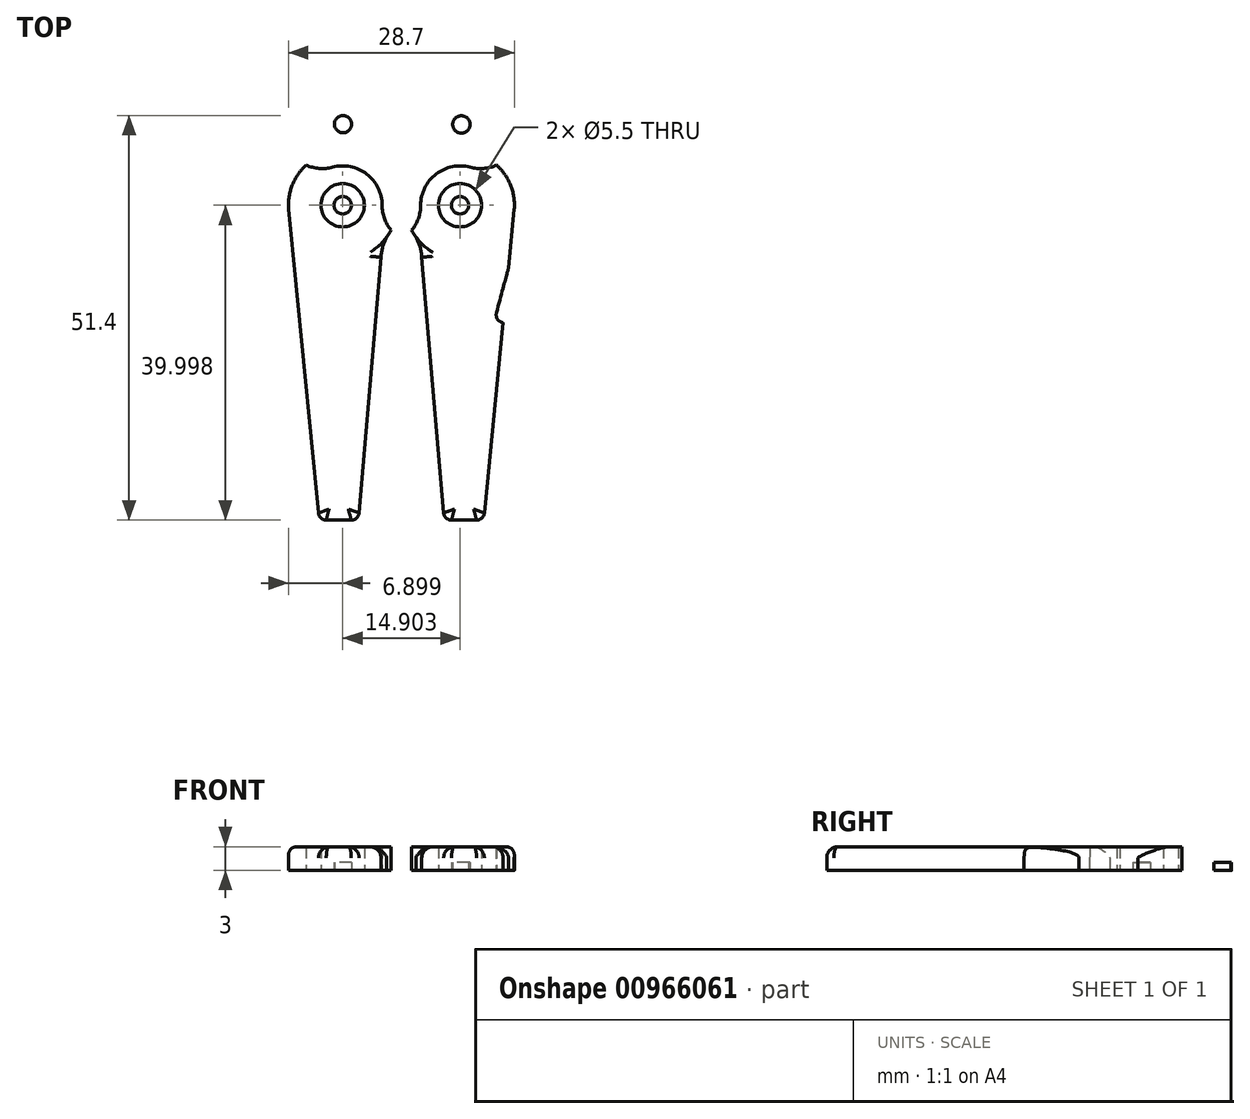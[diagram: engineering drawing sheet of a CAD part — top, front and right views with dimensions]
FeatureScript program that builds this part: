
annotation { "Feature Type Name" : "Feature", "Feature Type Description" : "" }
export const myFeature = defineFeature(function(context is Context, id is Id, definition is map)
    precondition{}
    {
        {
            var Q0;
            Q0=qCreatedBy(makeId("Top.planeOp"),FACE);
            var sketch = newSketch(context, id + "F0", { "sketchPlane" : qUnion([Q0])});
            skArc(sketch, "E0", {"start": v(1.32, 9.18) * mm, "mid": v(2.16, 10.67) * mm, "end": v(2.45, 12.35) * mm});
            skArc(sketch, "E1", {"start": v(1.32, 9.18) * mm, "mid": v(1.57, 8.73) * mm, "end": v(1.86, 8.3) * mm});
            skArc(sketch, "E2", {"start": v(2.59, 5.75) * mm, "mid": v(2.37, 7.07) * mm, "end": v(1.86, 8.3) * mm});
            skLineSegment(sketch, "E3", {"start": v(2.59, 5.75) * mm, "end": v(5.37, -26.74) * mm});
            skArc(sketch, "E4", {"start": v(5.37, -26.74) * mm, "mid": v(5.7, -27.39) * mm, "end": v(6.37, -27.65) * mm});
            skLineSegment(sketch, "E5", {"start": v(6.37, -27.65) * mm, "end": v(9.54, -27.65) * mm});
            skArc(sketch, "E6", {"start": v(9.54, -27.65) * mm, "mid": v(10.22, -27.4) * mm, "end": v(10.54, -26.75) * mm});
            skArc(sketch, "E7", {"start": v(8.75, 17.18) * mm, "mid": v(4.4, 16.31) * mm, "end": v(2.45, 12.35) * mm});
            skArc(sketch, "E8", {"start": v(14.3, 11.5) * mm, "mid": v(13.92, 14.74) * mm, "end": v(12.1, 17.45) * mm});
            skArc(sketch, "E9", {"start": v(8.75, 17.18) * mm, "mid": v(10.44, 17.02) * mm, "end": v(12.1, 17.45) * mm});
            skArc(sketch, "E10", {"start": v(12.07, -1.31) * mm, "mid": v(12.17, -2.07) * mm, "end": v(12.78, -2.54) * mm});
            skLineSegment(sketch, "E11", {"start": v(10.54, -26.75) * mm, "end": v(12.92, -2.57) * mm});
            skLineSegment(sketch, "E12", {"start": v(13.6, 4.38) * mm, "end": v(14.33, 11.86) * mm});
            skLineSegment(sketch, "E13", {"start": v(13.6, 4.38) * mm, "end": v(12.07, -1.31) * mm});
            skLineSegment(sketch, "E14", {"start": v(12.78, -2.54) * mm, "end": v(12.92, -2.57) * mm});
            skCircle(sketch, "E15", {"center": v(7.62, 22.62) * mm, "radius": 5 * mm});
            skCircle(sketch, "E16", {"center": v(7.45, 12.35) * mm, "radius": 1.1 * mm});
            skCircle(sketch, "E17", {"center": v(7.62, 22.62) * mm, "radius": 1.1 * mm});
            skArc(sketch, "E18", {"start": v(-2.45, 12.35) * mm, "mid": v(-2.16, 10.67) * mm, "end": v(-1.32, 9.18) * mm});
            skArc(sketch, "E19", {"start": v(-1.86, 8.3) * mm, "mid": v(-1.57, 8.73) * mm, "end": v(-1.32, 9.18) * mm});
            skArc(sketch, "E20", {"start": v(-1.86, 8.3) * mm, "mid": v(-2.37, 7.07) * mm, "end": v(-2.59, 5.75) * mm});
            skLineSegment(sketch, "E21", {"start": v(-2.59, 5.75) * mm, "end": v(-5.37, -26.74) * mm});
            skArc(sketch, "E22", {"start": v(-6.37, -27.65) * mm, "mid": v(-5.7, -27.39) * mm, "end": v(-5.37, -26.74) * mm});
            skLineSegment(sketch, "E23", {"start": v(-6.37, -27.65) * mm, "end": v(-9.54, -27.65) * mm});
            skLineSegment(sketch, "E24", {"start": v(-10.54, -26.75) * mm, "end": v(-14.33, 11.86) * mm});
            skArc(sketch, "E25", {"start": v(-10.54, -26.75) * mm, "mid": v(-10.22, -27.4) * mm, "end": v(-9.54, -27.65) * mm});
            skArc(sketch, "E26", {"start": v(-2.45, 12.35) * mm, "mid": v(-4.4, 16.31) * mm, "end": v(-8.75, 17.18) * mm});
            skArc(sketch, "E27", {"start": v(-12.1, 17.45) * mm, "mid": v(-13.92, 14.74) * mm, "end": v(-14.3, 11.5) * mm});
            skArc(sketch, "E28", {"start": v(-12.1, 17.45) * mm, "mid": v(-10.44, 17.02) * mm, "end": v(-8.75, 17.18) * mm});
            skCircle(sketch, "E29", {"center": v(-7.41, 22.65) * mm, "radius": 5 * mm});
            skCircle(sketch, "E30", {"center": v(-7.41, 22.65) * mm, "radius": 1.1 * mm});
            skCircle(sketch, "E31", {"center": v(-7.45, 12.35) * mm, "radius": 1.1 * mm});
            skCircle(sketch, "E32", {"center": v(-7.41, 22.65) * mm, "radius": 2.75 * mm});
            skCircle(sketch, "E33", {"center": v(-7.45, 12.35) * mm, "radius": 2.75 * mm});
            skCircle(sketch, "E34", {"center": v(7.45, 12.35) * mm, "radius": 2.75 * mm});
            skCircle(sketch, "E35", {"center": v(7.62, 22.62) * mm, "radius": 2.75 * mm});
            skSolve(sketch);
        }
        {
            var Q0;
            Q0=makeQuery(id+"F0.imprint","IMPRINT",FACE,{"disambiguationData":[TD([[makeQuery(id+"F0.imprint","IMPRINT",EDGE,{"derivedFrom":sQuery(id+"F0.wireOp",EDGE,"E18")}),-1.0]])]});
            var Q1;
            Q1=makeQuery(id+"F0.imprint","IMPRINT",FACE,{"disambiguationData":[TD([[makeQuery(id+"F0.imprint","IMPRINT",EDGE,{"derivedFrom":sQuery(id+"F0.wireOp",EDGE,"E0")}),-1.0]])]});
            var Q2;
            Q2=makeQuery(id+"F0.imprint","IMPRINT",FACE,{"disambiguationData":[TD([[makeQuery(id+"F0.imprint","IMPRINT",EDGE,{"derivedFrom":sQuery(id+"F0.wireOp",EDGE,"E15")}),-1.0]])]});
            var Q3;
            Q3=makeQuery(id+"F0.imprint","IMPRINT",FACE,{"disambiguationData":[TD([[makeQuery(id+"F0.imprint","IMPRINT",EDGE,{"derivedFrom":sQuery(id+"F0.wireOp",EDGE,"E29")}),-1.0]])]});
            extrude(context, id + "F1", {"entities" : qUnion([Q0, Q1, Q2, Q3]), "depth" : 3 * mm, "offsetDistance" : 25 * mm});
        }
        {
            var Q0;
            Q0=makeQuery(id+"F0.imprint","IMPRINT",FACE,{"disambiguationData":[TD([[makeQuery(id+"F0.imprint","IMPRINT",EDGE,{"derivedFrom":sQuery(id+"F0.wireOp",EDGE,"E30")}),1.0]])]});
            var Q1;
            Q1=makeQuery(id+"F0.imprint","IMPRINT",FACE,{"disambiguationData":[TD([[makeQuery(id+"F0.imprint","IMPRINT",EDGE,{"derivedFrom":sQuery(id+"F0.wireOp",EDGE,"E17")}),1.0]])]});
            var Q2;
            Q2=makeQuery(id+"F0.imprint","IMPRINT",FACE,{"disambiguationData":[TD([[makeQuery(id+"F0.imprint","IMPRINT",EDGE,{"derivedFrom":sQuery(id+"F0.wireOp",EDGE,"E16")}),1.0]])]});
            var Q3;
            Q3=makeQuery(id+"F0.imprint","IMPRINT",FACE,{"disambiguationData":[TD([[makeQuery(id+"F0.imprint","IMPRINT",EDGE,{"derivedFrom":sQuery(id+"F0.wireOp",EDGE,"E31")}),1.0]])]});
            extrude(context, id + "F2", {"entities" : qUnion([Q0, Q1, Q2, Q3]), "operationType" : NewBodyOperationType.ADD, "depth" : 1 * mm, "offsetDistance" : 25 * mm});
        }
        {
            var Q0;
            Q0=makeQuery(id+"F1.opExtrude","CAP_EDGE",EDGE,{"disambiguationData":[OSD([sQuery(id+"F0.wireOp",EDGE,"E15")])],"isStart":false});
            var Q1;
            Q1=makeQuery(id+"F1.opExtrude","CAP_EDGE",EDGE,{"disambiguationData":[OSD([sQuery(id+"F0.wireOp",EDGE,"E29")])],"isStart":false});
            var Q2;
            Q2=makeQuery(id+"F1.opExtrude","CAP_EDGE",EDGE,{"disambiguationData":[OSD([sQuery(id+"F0.wireOp",EDGE,"E21")])],"isStart":false});
            var Q3;
            Q3=makeQuery(id+"F1.opExtrude","CAP_EDGE",EDGE,{"disambiguationData":[OSD([sQuery(id+"F0.wireOp",EDGE,"E3")])],"isStart":false});
            fillet(context, id + "F3", {"entities" : qUnion([Q0, Q1, Q2, Q3]), "radius" : 1.4 * mm, "tangentPropagation" : true, "allowEdgeOverflow" : false});
        }
    });
